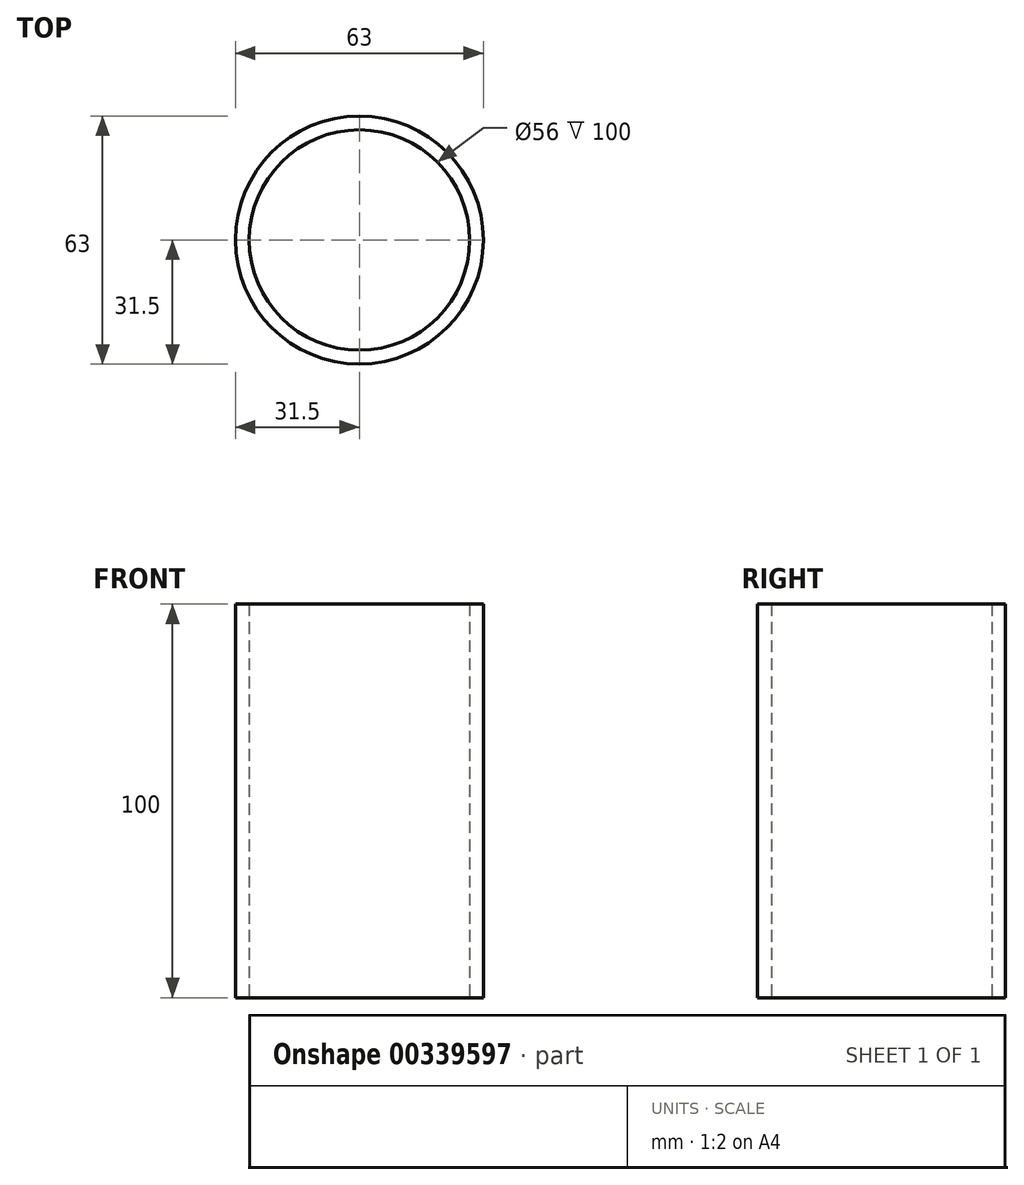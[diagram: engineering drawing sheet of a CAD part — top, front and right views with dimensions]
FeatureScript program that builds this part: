
annotation { "Feature Type Name" : "Feature", "Feature Type Description" : "" }
export const myFeature = defineFeature(function(context is Context, id is Id, definition is map)
    precondition{}
    {
        {
            var Q0;
            Q0=qCreatedBy(makeId("Top.planeOp"),FACE);
            var sketch = newSketch(context, id + "F0", { "sketchPlane" : qUnion([Q0])});
            skCircle(sketch, "E0", {"center": v(0, 0) * mm, "radius": 31.5 * mm});
            skCircle(sketch, "E1", {"center": v(0, 0) * mm, "radius": 28 * mm});
            skSolve(sketch);
        }
        {
            var Q0;
            Q0=makeQuery(id+"F0.imprint","IMPRINT",FACE,{"disambiguationData":[TD([[makeQuery(id+"F0.imprint","IMPRINT",EDGE,{"derivedFrom":sQuery(id+"F0.wireOp",EDGE,"E0")}),1.0]])]});
            extrude(context, id + "F1", {"entities" : qUnion([Q0]), "depth" : 100 * mm});
        }
    });
